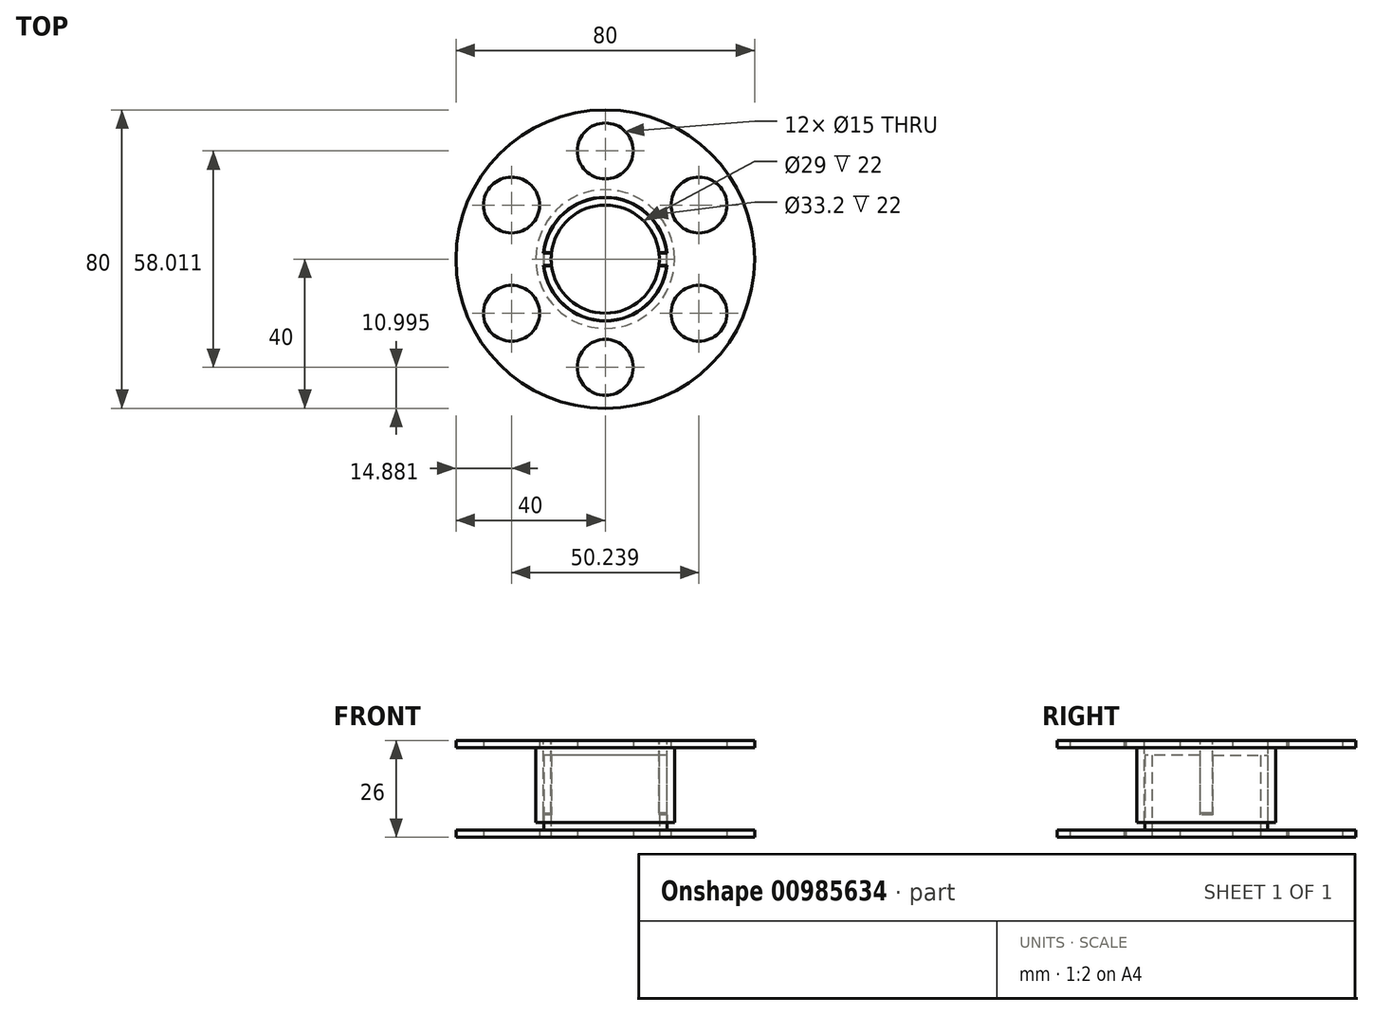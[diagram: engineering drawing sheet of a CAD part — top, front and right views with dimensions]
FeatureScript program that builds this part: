
annotation { "Feature Type Name" : "Feature", "Feature Type Description" : "" }
export const myFeature = defineFeature(function(context is Context, id is Id, definition is map)
    precondition{}
    {
        {
            var Q0;
            Q0=qCreatedBy(makeId("Top.planeOp"),FACE);
            var sketch = newSketch(context, id + "F0", { "sketchPlane" : qUnion([Q0])});
            skCircle(sketch, "E0", {"center": v(0, 0) * mm, "radius": 40 * mm});
            skLineSegment(sketch, "E1", {"start": v(0, 0) * mm, "end": v(0, 29) * mm, "construction": true});
            skCircle(sketch, "E2", {"center": v(0, 29) * mm, "radius": 7.5 * mm});
            skCircle(sketch, "E3.1.0", {"center": v(-25.12, 14.5) * mm, "radius": 7.5 * mm});
            skCircle(sketch, "E3.2.0", {"center": v(-25.12, -14.5) * mm, "radius": 7.5 * mm});
            skCircle(sketch, "E4.1.3.0", {"center": v(0, -29) * mm, "radius": 7.5 * mm});
            skCircle(sketch, "E4.1.4.0", {"center": v(25.12, -14.5) * mm, "radius": 7.5 * mm});
            skCircle(sketch, "E4.1.5.0", {"center": v(25.12, 14.5) * mm, "radius": 7.5 * mm});
            skCircle(sketch, "E5", {"center": v(0, 0) * mm, "radius": 14.5 * mm});
            skSolve(sketch);
        }
        {
            var Q0;
            Q0 = qSketchRegion(id + "F0", true);
            extrude(context, id + "F1", {"entities" : qUnion([Q0]), "depth" : 2 * mm, "offsetDistance" : 25 * mm});
        }
        {
            var Q0;
            Q0=makeQuery(id+"F1.opExtrude","CAP_FACE",FACE,{"disambiguationData":[OSD([sQuery(id+"F0.wireOp",EDGE,"E0"),sQuery(id+"F0.wireOp",EDGE,"E2"),sQuery(id+"F0.wireOp",EDGE,"E3.1.0"),sQuery(id+"F0.wireOp",EDGE,"E3.2.0"),sQuery(id+"F0.wireOp",EDGE,"E4.1.3.0"),sQuery(id+"F0.wireOp",EDGE,"E4.1.4.0"),sQuery(id+"F0.wireOp",EDGE,"E4.1.5.0"),sQuery(id+"F0.wireOp",EDGE,"E5")])],"isStart":false});
            var sketch = newSketch(context, id + "F2", { "sketchPlane" : qUnion([Q0])});
            skCircle(sketch, "E6.0", {"center": v(0, 0) * mm, "radius": 14.5 * mm});
            skCircle(sketch, "E7", {"center": v(0, 0) * mm, "radius": 16.5 * mm});
            skSolve(sketch);
        }
        {
            var Q0;
            Q0 = qSketchRegion(id + "F2", true);
            extrude(context, id + "F3", {"entities" : qUnion([Q0]), "operationType" : NewBodyOperationType.ADD, "depth" : 20 * mm, "offsetDistance" : 25 * mm});
        }
        {
            var Q0;
            Q0=makeQuery(id+"F3.opExtrude","CAP_FACE",FACE,{"disambiguationData":[OSD([sQuery(id+"F2.wireOp",EDGE,"E6.0"),sQuery(id+"F2.wireOp",EDGE,"E7")])],"isStart":false});
            var sketch = newSketch(context, id + "F4", { "sketchPlane" : qUnion([Q0])});
            skLineSegment(sketch, "E8.bottom", {"start": v(20, -1.75) * mm, "end": v(-20, -1.75) * mm});
            skLineSegment(sketch, "E8.top", {"start": v(20, 1.75) * mm, "end": v(-20, 1.75) * mm});
            skLineSegment(sketch, "E8.left", {"start": v(20, -1.75) * mm, "end": v(20, 1.75) * mm});
            skLineSegment(sketch, "E8.right", {"start": v(-20, -1.75) * mm, "end": v(-20, 1.75) * mm});
            skPoint(sketch, "E8.middle", {"position": v(0, 0) * mm});
            skSolve(sketch);
        }
        {
            var Q0;
            Q0 = qSketchRegion(id + "F4", true);
            extrude(context, id + "F5", {"entities" : qUnion([Q0]), "operationType" : NewBodyOperationType.REMOVE, "oppositeDirection" : true, "depth" : 16 * mm, "offsetDistance" : 25 * mm});
        }
        {
            var Q0;
            Q0=makeQuery(id+"F1.opExtrude","CAP_FACE",FACE,{"disambiguationData":[OSD([sQuery(id+"F0.wireOp",EDGE,"E0"),sQuery(id+"F0.wireOp",EDGE,"E2"),sQuery(id+"F0.wireOp",EDGE,"E3.1.0"),sQuery(id+"F0.wireOp",EDGE,"E3.2.0"),sQuery(id+"F0.wireOp",EDGE,"E4.1.3.0"),sQuery(id+"F0.wireOp",EDGE,"E4.1.4.0"),sQuery(id+"F0.wireOp",EDGE,"E4.1.5.0"),sQuery(id+"F0.wireOp",EDGE,"E5")])],"isStart":false});
            cPlane(context, id + "F6", {"entities" : qUnion([Q0]), "cplaneType" : CPlaneType.OFFSET, "offset" : 22 * mm, "width" : 150 * mm, "height" : 150 * mm});
        }
        {
            var Q0;
            Q0=qCreatedBy(id+"F6.planeOp",FACE);
            var sketch = newSketch(context, id + "F7", { "sketchPlane" : qUnion([Q0])});
            skArc(sketch, "E9.0", {"start": v(-16.4, -1.75) * mm, "mid": v(0, -16.5) * mm, "end": v(16.4, -1.75) * mm, "construction": true});
            skCircle(sketch, "E10", {"center": v(0, 0) * mm, "radius": 16.6 * mm});
            skCircle(sketch, "E11", {"center": v(0, 0) * mm, "radius": 18.6 * mm});
            skSolve(sketch);
        }
        {
            var Q0;
            Q0 = qSketchRegion(id + "F7", true);
            extrude(context, id + "F8", {"entities" : qUnion([Q0]), "oppositeDirection" : true, "depth" : 20 * mm, "offsetDistance" : 25 * mm});
        }
        {
            var Q0;
            Q0=qCreatedBy(id+"F6.planeOp",FACE);
            var sketch = newSketch(context, id + "F9", { "sketchPlane" : qUnion([Q0])});
            skCircle(sketch, "E12.0", {"center": v(0, 0) * mm, "radius": 16.6 * mm});
            skCircle(sketch, "E13.0", {"center": v(0, 0) * mm, "radius": 40 * mm});
            skCircle(sketch, "E14.0", {"center": v(0, 29) * mm, "radius": 7.5 * mm});
            skCircle(sketch, "E15.0", {"center": v(25.12, 14.5) * mm, "radius": 7.5 * mm});
            skCircle(sketch, "E16.0", {"center": v(25.12, -14.5) * mm, "radius": 7.5 * mm});
            skCircle(sketch, "E17.0", {"center": v(0, -29) * mm, "radius": 7.5 * mm});
            skCircle(sketch, "E18.0", {"center": v(-25.12, -14.5) * mm, "radius": 7.5 * mm});
            skCircle(sketch, "E19.0", {"center": v(-25.12, 14.5) * mm, "radius": 7.5 * mm});
            skSolve(sketch);
        }
        {
            var Q0;
            Q0 = qSketchRegion(id + "F9", true);
            extrude(context, id + "F10", {"entities" : qUnion([Q0]), "operationType" : NewBodyOperationType.ADD, "depth" : 2 * mm, "offsetDistance" : 25 * mm});
        }
        {
            var Q0;
            Q0=makeQuery(id+"F10.opExtrude","CAP_FACE",FACE,{"disambiguationData":[OSD([sQuery(id+"F9.wireOp",EDGE,"E12.0"),sQuery(id+"F9.wireOp",EDGE,"E13.0"),sQuery(id+"F9.wireOp",EDGE,"E14.0"),sQuery(id+"F9.wireOp",EDGE,"E15.0"),sQuery(id+"F9.wireOp",EDGE,"E16.0"),sQuery(id+"F9.wireOp",EDGE,"E17.0"),sQuery(id+"F9.wireOp",EDGE,"E18.0"),sQuery(id+"F9.wireOp",EDGE,"E19.0")])],"isStart":false});
            var sketch = newSketch(context, id + "F11", { "sketchPlane" : qUnion([Q0])});
            skLineSegment(sketch, "E20.0", {"start": v(16.74, 1.75) * mm, "end": v(14.4, 1.75) * mm, "construction": true});
            skLineSegment(sketch, "E21.0", {"start": v(16.74, -1.75) * mm, "end": v(14.4, -1.75) * mm, "construction": true});
            skPoint(sketch, "E22.orphan", {"position": v(16.4, 1.75) * mm});
            skPoint(sketch, "E23.orphan", {"position": v(16.4, -1.75) * mm});
            skLineSegment(sketch, "E24", {"start": v(14.4, 1.65) * mm, "end": v(16.52, 1.65) * mm});
            skLineSegment(sketch, "E25.MirrorCS", {"start": v(14.4, -1.65) * mm, "end": v(16.52, -1.65) * mm});
            skArc(sketch, "E26.0", {"start": v(14.4, -1.65) * mm, "mid": v(14.5, 0) * mm, "end": v(14.4, 1.65) * mm});
            skPoint(sketch, "E27.orphan", {"position": v(14.4, 1.75) * mm});
            skPoint(sketch, "E28.orphan", {"position": v(14.4, 1.65) * mm});
            skPoint(sketch, "E29.orphan", {"position": v(14.4, -1.75) * mm});
            skPoint(sketch, "E30.orphan", {"position": v(14.4, -1.65) * mm});
            skArc(sketch, "E31.trimOffspring", {"start": v(16.52, -1.65) * mm, "mid": v(16.6, 0) * mm, "end": v(16.52, 1.65) * mm});
            skLineSegment(sketch, "E32.MirrorCS", {"start": v(-14.4, 1.65) * mm, "end": v(-16.52, 1.65) * mm});
            skLineSegment(sketch, "E33.MirrorCS", {"start": v(-14.4, -1.65) * mm, "end": v(-16.52, -1.65) * mm});
            skLineSegment(sketch, "E34.MirrorCS", {"start": v(-16.74, 1.75) * mm, "end": v(-14.4, 1.75) * mm, "construction": true});
            skPoint(sketch, "E35.MirrorP", {"position": v(-14.4, 1.65) * mm});
            skLineSegment(sketch, "E36.MirrorCS", {"start": v(-16.74, -1.75) * mm, "end": v(-14.4, -1.75) * mm, "construction": true});
            skPoint(sketch, "E37.MirrorP", {"position": v(-14.4, -1.65) * mm});
            skPoint(sketch, "E38.MirrorP", {"position": v(-16.4, 1.75) * mm});
            skPoint(sketch, "E39.MirrorP", {"position": v(-14.4, 1.75) * mm});
            skPoint(sketch, "E40.MirrorP", {"position": v(-14.4, -1.75) * mm});
            skArc(sketch, "E41.MirrorCS", {"start": v(-14.4, -1.65) * mm, "mid": v(-14.5, 0) * mm, "end": v(-14.4, 1.65) * mm});
            skPoint(sketch, "E42.MirrorP", {"position": v(-16.4, -1.75) * mm});
            skArc(sketch, "E43.MirrorCS", {"start": v(-16.52, -1.65) * mm, "mid": v(-16.6, 0) * mm, "end": v(-16.52, 1.65) * mm});
            skSolve(sketch);
        }
        {
            var Q0;
            Q0 = qSketchRegion(id + "F11", true);
            var Q1;
            Q1=makeQuery(id+"F5.boolean.opBoolean","COPY",FACE,{"disambiguationData":[OD(0.0)],"derivedFrom":makeQuery(id+"F5.opExtrude","CAP_FACE",FACE,{"disambiguationData":[OSD([sQuery(id+"F4.wireOp",EDGE,"E8.bottom"),sQuery(id+"F4.wireOp",EDGE,"E8.top"),sQuery(id+"F4.wireOp",EDGE,"E8.left"),sQuery(id+"F4.wireOp",EDGE,"E8.right")])],"isStart":false})});
            extrude(context, id + "F12", {"entities" : qUnion([Q0]), "operationType" : NewBodyOperationType.ADD, "endBound" : BoundingType.UP_TO_SURFACE, "oppositeDirection" : true, "depth" : 25 * mm, "endBoundEntityFace" : qUnion([Q1]), "hasOffset" : true, "offsetDistance" : .5 * mm});
        }
        {
            var Q0;
            Q0 = qSketchRegion(id + "F11", true);
            extrude(context, id + "F13", {"entities" : qUnion([Q0]), "operationType" : NewBodyOperationType.ADD, "oppositeDirection" : true, "depth" : 16 * mm, "offsetDistance" : 25 * mm});
        }
    });
